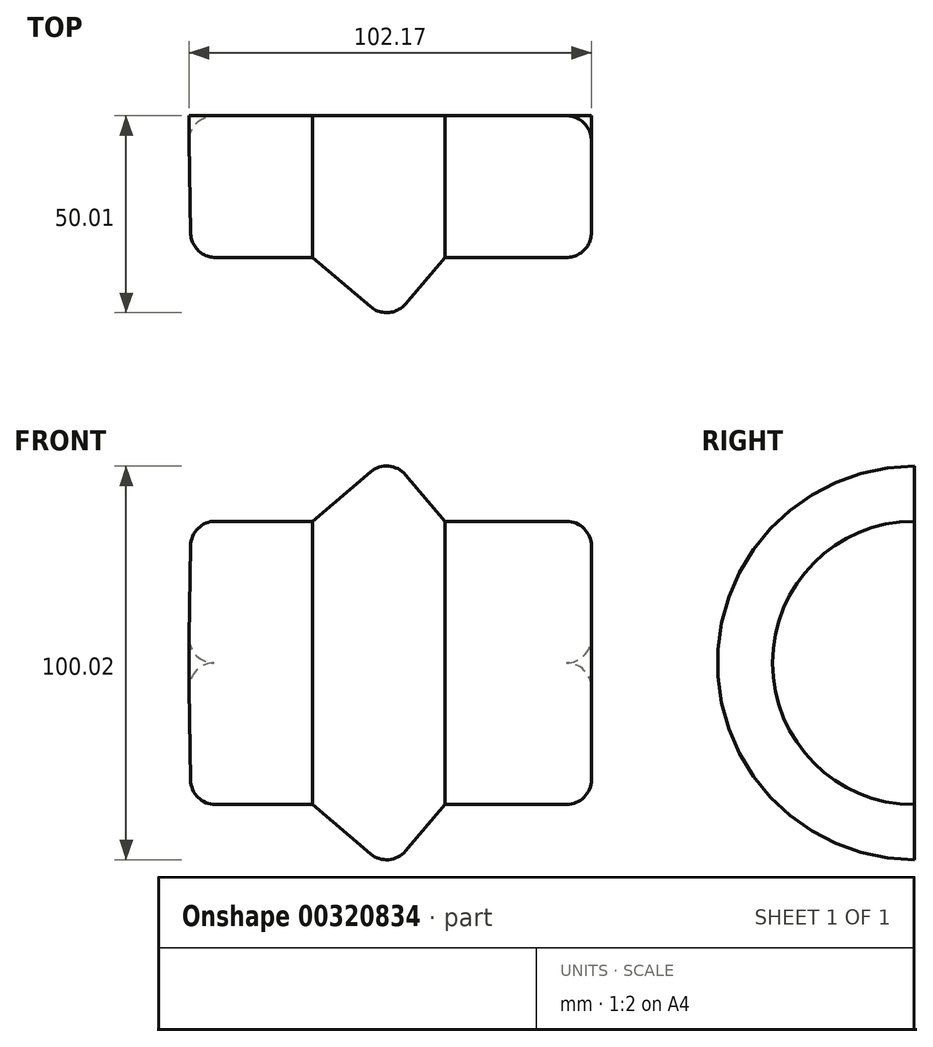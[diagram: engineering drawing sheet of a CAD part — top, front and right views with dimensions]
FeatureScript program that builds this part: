
annotation { "Feature Type Name" : "Feature", "Feature Type Description" : "" }
export const myFeature = defineFeature(function(context is Context, id is Id, definition is map)
    precondition{}
    {
        {
            var Q0;
            Q0=qCreatedBy(makeId("Front.planeOp"),FACE);
            var sketch = newSketch(context, id + "F0", { "sketchPlane" : qUnion([Q0])});
            skLineSegment(sketch, "E0", {"start": v(-44.52, 0) * mm, "end": v(-30.31, 0) * mm});
            skLineSegment(sketch, "E1", {"start": v(-30.31, 0) * mm, "end": v(-3.53, 18.93) * mm});
            skLineSegment(sketch, "E2", {"start": v(3.62, 19.05) * mm, "end": v(32.65, 0) * mm});
            skLineSegment(sketch, "E3", {"start": v(32.65, 0) * mm, "end": v(44.95, 0) * mm});
            skLineSegment(sketch, "E4", {"start": v(51.3, 6.35) * mm, "end": v(51.3, 29.65) * mm});
            skLineSegment(sketch, "E5", {"start": v(-50.52, 29.74) * mm, "end": v(-50.87, 6.45) * mm});
            skLineSegment(sketch, "E6", {"start": v(-19.53, 36) * mm, "end": v(-4.84, 48.5) * mm});
            skLineSegment(sketch, "E7", {"start": v(4.11, 47.77) * mm, "end": v(14.13, 36) * mm});
            skLineSegment(sketch, "E8.trimOffspring", {"start": v(-19.53, 36) * mm, "end": v(-44.17, 36) * mm});
            skPoint(sketch, "E9.orphan", {"position": v(-51, -2.48) * mm});
            skLineSegment(sketch, "E10", {"start": v(14.13, 36) * mm, "end": v(44.95, 36) * mm});
            skLineSegment(sketch, "E11", {"start": v(-30.31, 0) * mm, "end": v(32.65, 0) * mm});
            skPoint(sketch, "E12.visualSharp", {"position": v(0, 52.61) * mm});
            skArc(sketch, "E12.filletArc", {"start": v(4.11, 47.77) * mm, "mid": v(-0.21, 49.99) * mm, "end": v(-4.84, 48.5) * mm});
            skPoint(sketch, "E13.visualSharp", {"position": v(-50.43, 36) * mm});
            skArc(sketch, "E13.filletArc", {"start": v(-44.17, 36) * mm, "mid": v(-48.63, 34.17) * mm, "end": v(-50.52, 29.74) * mm});
            skPoint(sketch, "E14.visualSharp", {"position": v(51.3, 36) * mm});
            skArc(sketch, "E14.filletArc", {"start": v(51.3, 29.65) * mm, "mid": v(49.44, 34.14) * mm, "end": v(44.95, 36) * mm});
            skPoint(sketch, "E15.newPointB", {"position": v(-51, 0) * mm});
            skArc(sketch, "E15.filletArc", {"start": v(-50.87, 6.45) * mm, "mid": v(-49.05, 1.9) * mm, "end": v(-44.52, 0) * mm});
            skPoint(sketch, "E16.visualSharp", {"position": v(51.3, 0) * mm});
            skArc(sketch, "E16.filletArc", {"start": v(44.95, 0) * mm, "mid": v(49.44, 1.86) * mm, "end": v(51.3, 6.35) * mm});
            skPoint(sketch, "E17.visualSharp", {"position": v(0, 21.42) * mm});
            skArc(sketch, "E17.filletArc", {"start": v(3.62, 19.05) * mm, "mid": v(0.02, 20.1) * mm, "end": v(-3.53, 18.93) * mm});
            skSolve(sketch);
        }
        {
            var Q0;
            {var subQ0=sQuery(id+"F0.wireOp",EDGE,"E1");Q0=makeQuery(id+"F0.imprint","IMPRINT",FACE,{"disambiguationData":[TD([[makeQuery(id+"F0.imprint","IMPRINT",EDGE,{"derivedFrom":subQ0}),1.0]])]});}
            var Q1;
            Q1=makeQuery(id+"F0.imprint","IMPRINT",FACE,{"disambiguationData":[TD([[makeQuery(id+"F0.imprint","IMPRINT",EDGE,{"derivedFrom":sQuery(id+"F0.wireOp",EDGE,"E1")}),-1.0]])]});
            var Q2;
            Q2=sQuery(id+"F0.wireOp",EDGE,"E11");
            revolve(context, id + "F1", {"entities" : qUnion([Q0, Q1]), "axis" : qUnion([Q2]), "revolveType" : RevolveType.ONE_DIRECTION, "angle" : 180 * degree});
        }
    });
